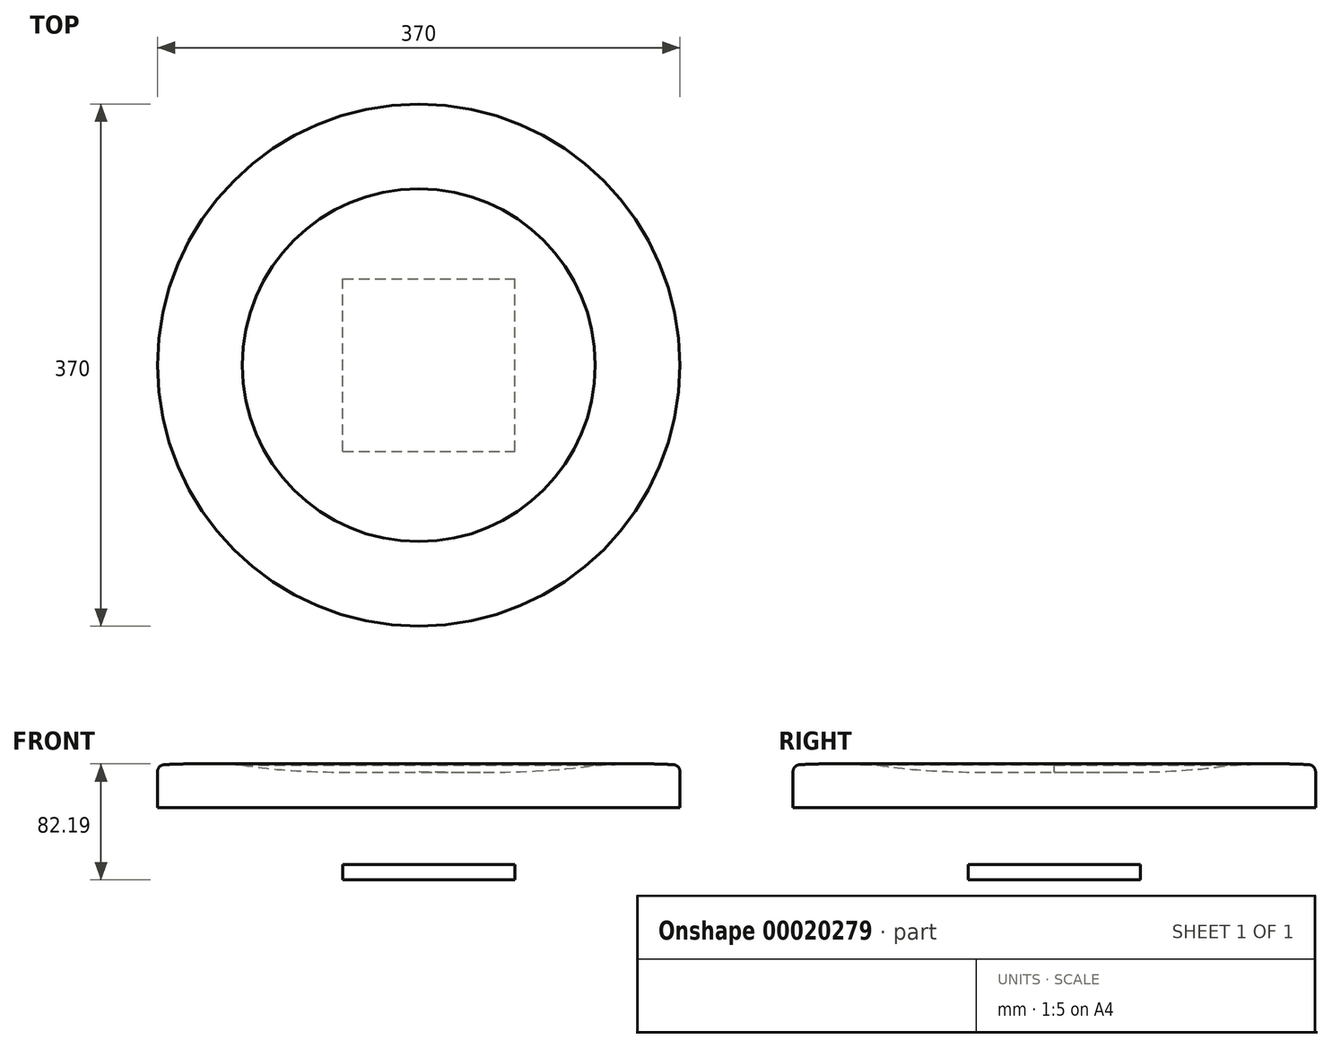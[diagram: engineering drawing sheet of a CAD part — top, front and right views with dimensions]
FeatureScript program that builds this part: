
annotation { "Feature Type Name" : "Feature", "Feature Type Description" : "" }
export const myFeature = defineFeature(function(context is Context, id is Id, definition is map)
    precondition{}
    {
        {
            var Q0;
            Q0=qCreatedBy(makeId("Front.planeOp"),FACE);
            var sketch = newSketch(context, id + "F0", { "sketchPlane" : qUnion([Q0])});
            skLineSegment(sketch, "E0.rect.bottom", {"start": v(61, -61) * mm, "end": v(-61, -61) * mm});
            skLineSegment(sketch, "E0.rect.top", {"start": v(61, 61) * mm, "end": v(-61, 61) * mm});
            skLineSegment(sketch, "E0.rect.left", {"start": v(61, -61) * mm, "end": v(61, 61) * mm});
            skLineSegment(sketch, "E0.rect.right", {"start": v(-61, -61) * mm, "end": v(-61, 61) * mm});
            skPoint(sketch, "E0.rect.middle", {"position": v(0, 0) * mm});
            skSolve(sketch);
        }
        {
            var Q0;
            Q0=makeQuery(id+"F0.imprint","IMPRINT",FACE,{"disambiguationData":[TD([[makeQuery(id+"F0.imprint","IMPRINT",EDGE,{"derivedFrom":sQuery(id+"F0.wireOp",EDGE,"E0.rect.bottom")}),-1.0]])]});
            extrude(context, id + "F1", {"entities" : qUnion([Q0]), "depth" : 6 * mm});
        }
        {
            var Q0;
            Q0=makeQuery(id+"F1.opExtrude","CAP_FACE",FACE,{"disambiguationData":[OSD([sQuery(id+"F0.wireOp",EDGE,"E0.rect.bottom"),sQuery(id+"F0.wireOp",EDGE,"E0.rect.top"),sQuery(id+"F0.wireOp",EDGE,"E0.rect.left"),sQuery(id+"F0.wireOp",EDGE,"E0.rect.right")])],"isStart":false});
            var sketch = newSketch(context, id + "F2", { "sketchPlane" : qUnion([Q0])});
            skLineSegment(sketch, "E1", {"start": v(-61, 0) * mm, "end": v(61, 0) * mm});
            skSolve(sketch);
        }
        {
            var Q0;
            Q0=makeQuery(id+"F1.opExtrude","SWEPT_BODY",BODY,{"disambiguationData":[OSD([sQuery(id+"F0.wireOp",EDGE,"E0.rect.bottom"),sQuery(id+"F0.wireOp",EDGE,"E0.rect.top"),sQuery(id+"F0.wireOp",EDGE,"E0.rect.left"),sQuery(id+"F0.wireOp",EDGE,"E0.rect.right")])]});
            var Q1;
            Q1=sQuery(id+"F2.wireOp",EDGE,"E1");
            transform(context, id + "F3", {"entities" : qUnion([Q0]), "transformType" : TransformType.ROTATION, "transformAxis" : qUnion([Q1]), "angle" : 90 * degree, "makeCopy" : false});
        }
        {
            var Q0;
            Q0=qCreatedBy(makeId("Front.planeOp"),FACE);
            var sketch = newSketch(context, id + "F4", { "sketchPlane" : qUnion([Q0])});
            skLineSegment(sketch, "E2", {"start": v(0, 0) * mm, "end": v(0, 25.5) * mm});
            skLineSegment(sketch, "E3", {"start": v(185, 0) * mm, "end": v(185, 25.35) * mm});
            skPoint(sketch, "E4", {"position": v(125, 0) * mm});
            skPoint(sketch, "E5", {"position": v(125, 30) * mm});
            skFitSpline(sketch, "E6", {"points": [v(0, 25.5) * mm, v(125, 30) * mm, v(229.2, 59.4) * mm], "startDerivative": vector(247.8, -4.87) * mm, "endDerivative": vector(210.14, 73.63) * mm});
            skFitSpline(sketch, "E7", {"points": [v(125, 30) * mm, v(185, 30) * mm, v(236.33, 21.37) * mm], "startDerivative": vector(118.33, 4.64) * mm, "endDerivative": vector(104.16, -22.22) * mm});
            skLineSegment(sketch, "E8", {"start": v(0, 0) * mm, "end": v(185, 0) * mm});
            skArc(sketch, "E9.filletArc", {"start": v(185, 25.35) * mm, "mid": v(183.65, 28.78) * mm, "end": v(180.32, 30.34) * mm});
            skSolve(sketch);
        }
        {
            var Q0;
            Q0=makeQuery(id+"F4.imprint","IMPRINT",FACE,{"disambiguationData":[TD([[makeQuery(id+"F4.imprint","IMPRINT",EDGE,{"derivedFrom":sQuery(id+"F4.wireOp",EDGE,"E2")}),-1.0]])]});
            var sketch = newSketch(context, id + "F5", { "sketchPlane" : qUnion([Q0])});
            skLineSegment(sketch, "E10", {"start": v(0, 0) * mm, "end": v(0, 28.9) * mm});
            skSolve(sketch);
        }
        {
            var Q0;
            Q0=makeQuery(id+"F4.imprint","IMPRINT",FACE,{"disambiguationData":[TD([[makeQuery(id+"F4.imprint","IMPRINT",EDGE,{"derivedFrom":sQuery(id+"F4.wireOp",EDGE,"E2")}),-1.0]])]});
            var Q1;
            Q1=sQuery(id+"F4.wireOp",EDGE,"E2");
            revolve(context, id + "F6", {"operationType" : NewBodyOperationType.ADD, "entities" : qUnion([Q0]), "axis" : qUnion([Q1]), "revolveType" : RevolveType.FULL});
        }
        {
            var Q0;
            Q0=makeQuery(id+"F1.opExtrude","SWEPT_BODY",BODY,{"disambiguationData":[OSD([sQuery(id+"F0.wireOp",EDGE,"E0.rect.bottom"),sQuery(id+"F0.wireOp",EDGE,"E0.rect.top"),sQuery(id+"F0.wireOp",EDGE,"E0.rect.left"),sQuery(id+"F0.wireOp",EDGE,"E0.rect.right")])]});
            var Q1;
            Q1=sQuery(id+"F5.wireOp",EDGE,"E10");
            transform(context, id + "F7", {"entities" : qUnion([Q0]), "transformType" : TransformType.TRANSLATION_DISTANCE, "transformDirection" : qUnion([Q1]), "distance" : 46.73 * mm, "makeCopy" : false});
        }
        {
            var Q0;
            Q0=qCreatedBy(makeId("Front.planeOp"),FACE);
            var sketch = newSketch(context, id + "F8", { "sketchPlane" : qUnion([Q0])});
            skLineSegment(sketch, "E11.bottom", {"start": v(-53.86, 6.2) * mm, "end": v(68.14, 6.2) * mm});
            skLineSegment(sketch, "E11.top", {"start": v(-53.86, -4.54) * mm, "end": v(68.14, -4.54) * mm});
            skLineSegment(sketch, "E11.left", {"start": v(-53.86, 6.2) * mm, "end": v(-53.86, -4.54) * mm});
            skLineSegment(sketch, "E11.right", {"start": v(68.14, 6.2) * mm, "end": v(68.14, -4.54) * mm});
            skSolve(sketch);
        }
        {
            var Q0;
            Q0=makeQuery(id+"F8.imprint","IMPRINT",FACE,{"disambiguationData":[TD([[makeQuery(id+"F8.imprint","IMPRINT",EDGE,{"derivedFrom":sQuery(id+"F8.wireOp",EDGE,"E11.bottom")}),-1.0]])]});
            extrude(context, id + "F9", {"entities" : qUnion([Q0]), "endBound" : BoundingType.SYMMETRIC, "depth" : 122 * mm});
        }
    });
